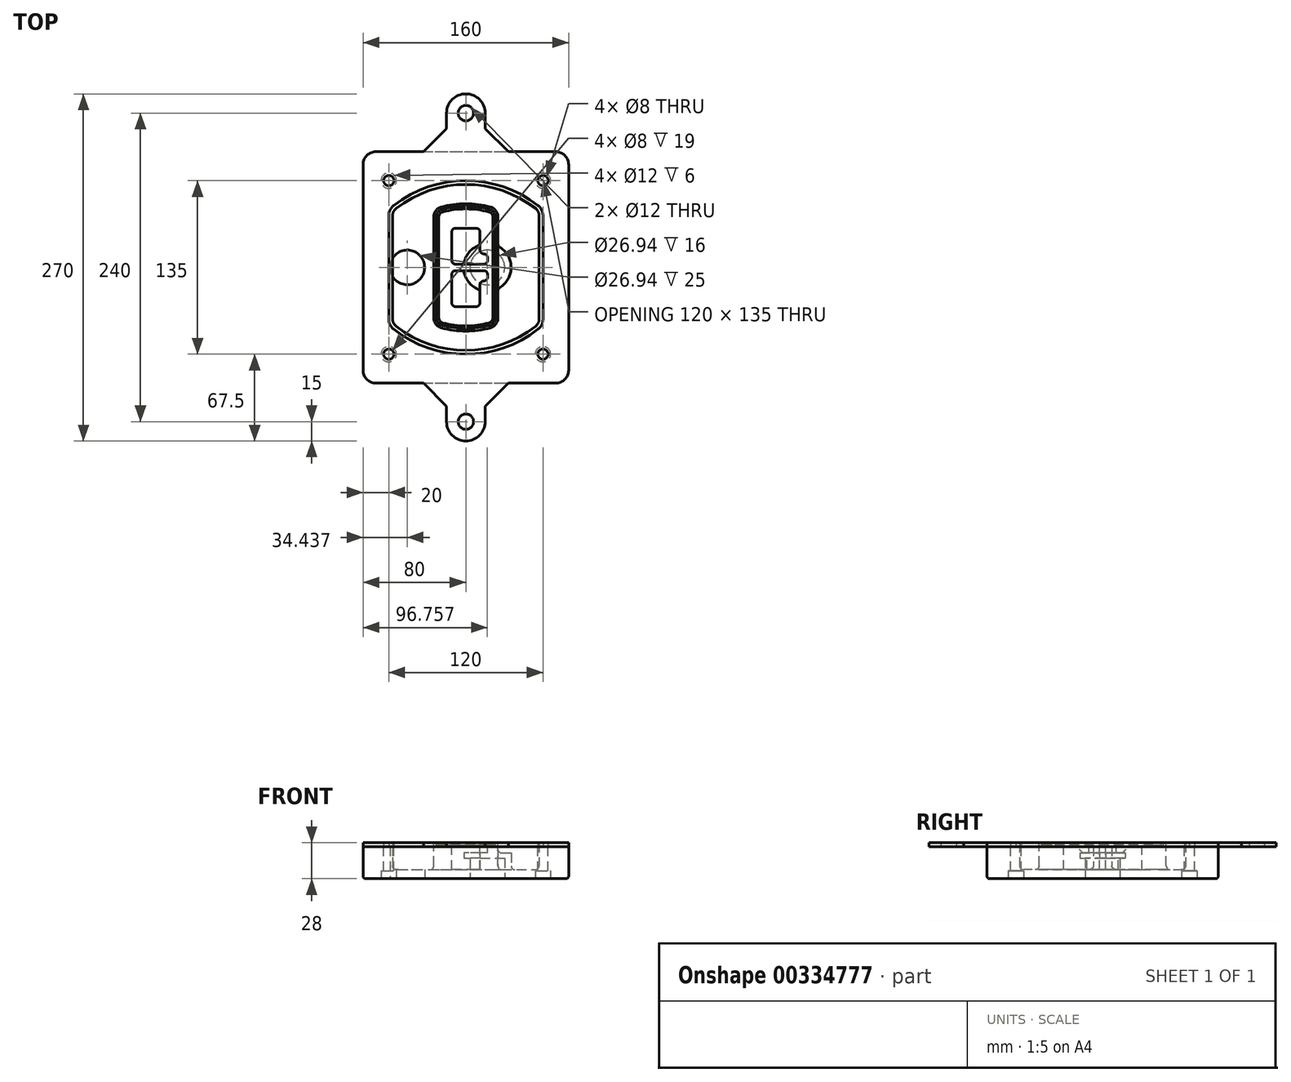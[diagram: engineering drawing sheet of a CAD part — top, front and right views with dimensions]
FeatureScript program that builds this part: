
annotation { "Feature Type Name" : "Feature", "Feature Type Description" : "" }
export const myFeature = defineFeature(function(context is Context, id is Id, definition is map)
    precondition{}
    {
        {
            var Q0;
            Q0=qCreatedBy(makeId("Top.planeOp"),FACE);
            var sketch = newSketch(context, id + "F0", { "sketchPlane" : qUnion([Q0])});
            skPoint(sketch, "E0.rect.middle", {"position": v(0, 0) * mm});
            skLineSegment(sketch, "E1.bottom", {"start": v(-70, -90) * mm, "end": v(70, -90) * mm});
            skLineSegment(sketch, "E1.top", {"start": v(-70, 90) * mm, "end": v(70, 90) * mm});
            skLineSegment(sketch, "E1.left", {"start": v(-80, -80) * mm, "end": v(-80, 80) * mm});
            skLineSegment(sketch, "E1.right", {"start": v(80, -80) * mm, "end": v(80, 80) * mm});
            skLineSegment(sketch, "E2", {"start": v(-80, 90) * mm, "end": v(80, -90) * mm, "construction": true});
            skLineSegment(sketch, "E3", {"start": v(80, 90) * mm, "end": v(-80, -90) * mm, "construction": true});
            skCircle(sketch, "E4", {"center": v(-60, 67.5) * mm, "radius": 4 * mm});
            skCircle(sketch, "E5", {"center": v(60, 67.5) * mm, "radius": 4 * mm});
            skCircle(sketch, "E6", {"center": v(60, -67.5) * mm, "radius": 4 * mm});
            skCircle(sketch, "E7", {"center": v(-60, -67.5) * mm, "radius": 4 * mm});
            skLineSegment(sketch, "E8", {"start": v(-60, 67.5) * mm, "end": v(60, 67.5) * mm, "construction": true});
            skLineSegment(sketch, "E9", {"start": v(60, 67.5) * mm, "end": v(60, -67.5) * mm, "construction": true});
            skLineSegment(sketch, "E10", {"start": v(60, -67.5) * mm, "end": v(-60, -67.5) * mm, "construction": true});
            skLineSegment(sketch, "E11", {"start": v(-60, -67.5) * mm, "end": v(-60, 67.5) * mm, "construction": true});
            skLineSegment(sketch, "E12", {"start": v(-60, 40.3) * mm, "end": v(-60, -40.3) * mm});
            skLineSegment(sketch, "E13", {"start": v(60, 40.3) * mm, "end": v(60, -40.3) * mm});
            skArc(sketch, "E14", {"start": v(56.15, 48.18) * mm, "mid": v(0, 67.5) * mm, "end": v(-56.15, 48.18) * mm});
            skArc(sketch, "E15", {"start": v(-56.15, -48.18) * mm, "mid": v(0, -67.5) * mm, "end": v(56.15, -48.18) * mm});
            skLineSegment(sketch, "E16", {"start": v(-60, 0) * mm, "end": v(60, 0) * mm, "construction": true});
            skPoint(sketch, "E17.visualSharp", {"position": v(-60, -45) * mm});
            skArc(sketch, "E17.filletArc", {"start": v(-60, -40.3) * mm, "mid": v(-58.99, -44.68) * mm, "end": v(-56.15, -48.18) * mm});
            skPoint(sketch, "E18.visualSharp", {"position": v(-60, 45) * mm});
            skArc(sketch, "E18.filletArc", {"start": v(-56.15, 48.18) * mm, "mid": v(-58.99, 44.68) * mm, "end": v(-60, 40.3) * mm});
            skPoint(sketch, "E19.visualSharp", {"position": v(60, 45) * mm});
            skArc(sketch, "E19.filletArc", {"start": v(60, 40.3) * mm, "mid": v(58.99, 44.68) * mm, "end": v(56.15, 48.18) * mm});
            skPoint(sketch, "E20.visualSharp", {"position": v(60, -45) * mm});
            skArc(sketch, "E20.filletArc", {"start": v(56.15, -48.18) * mm, "mid": v(58.99, -44.68) * mm, "end": v(60, -40.3) * mm});
            skPoint(sketch, "E21.visualSharp", {"position": v(-80, 90) * mm});
            skArc(sketch, "E21.filletArc", {"start": v(-70, 90) * mm, "mid": v(-77.07, 87.07) * mm, "end": v(-80, 80) * mm});
            skPoint(sketch, "E22.visualSharp", {"position": v(80, 90) * mm});
            skArc(sketch, "E22.filletArc", {"start": v(80, 80) * mm, "mid": v(77.07, 87.07) * mm, "end": v(70, 90) * mm});
            skPoint(sketch, "E23.visualSharp", {"position": v(80, -90) * mm});
            skArc(sketch, "E23.filletArc", {"start": v(70, -90) * mm, "mid": v(77.07, -87.07) * mm, "end": v(80, -80) * mm});
            skPoint(sketch, "E24.visualSharp", {"position": v(-80, -90) * mm});
            skArc(sketch, "E24.filletArc", {"start": v(-80, -80) * mm, "mid": v(-77.07, -87.07) * mm, "end": v(-70, -90) * mm});
            skArc(sketch, "E25.0", {"start": v(57, 40.3) * mm, "mid": v(56.3, 43.36) * mm, "end": v(54.3, 45.81) * mm});
            skLineSegment(sketch, "E25.1", {"start": v(57, 40.3) * mm, "end": v(57, -40.3) * mm});
            skArc(sketch, "E25.2", {"start": v(54.3, -45.81) * mm, "mid": v(56.3, -43.36) * mm, "end": v(57, -40.3) * mm});
            skArc(sketch, "E25.3", {"start": v(-54.3, -45.81) * mm, "mid": v(0, -64.5) * mm, "end": v(54.3, -45.81) * mm});
            skArc(sketch, "E25.4", {"start": v(-57, -40.3) * mm, "mid": v(-56.3, -43.36) * mm, "end": v(-54.3, -45.81) * mm});
            skArc(sketch, "E25.5", {"start": v(54.3, 45.81) * mm, "mid": v(0, 64.5) * mm, "end": v(-54.3, 45.81) * mm});
            skLineSegment(sketch, "E25.6", {"start": v(-57, 40.3) * mm, "end": v(-57, -40.3) * mm});
            skArc(sketch, "E25.7", {"start": v(-54.3, 45.81) * mm, "mid": v(-56.3, 43.36) * mm, "end": v(-57, 40.3) * mm});
            skArc(sketch, "E26.0", {"start": v(-58.62, 51.33) * mm, "mid": v(-62.58, 46.43) * mm, "end": v(-64, 40.3) * mm});
            skArc(sketch, "E26.1", {"start": v(58.62, 51.33) * mm, "mid": v(0, 71.5) * mm, "end": v(-58.62, 51.33) * mm});
            skArc(sketch, "E26.2", {"start": v(64, 40.3) * mm, "mid": v(62.58, 46.43) * mm, "end": v(58.62, 51.33) * mm});
            skLineSegment(sketch, "E26.3", {"start": v(64, 40.3) * mm, "end": v(64, -40.3) * mm});
            skArc(sketch, "E26.4", {"start": v(58.62, -51.33) * mm, "mid": v(62.58, -46.43) * mm, "end": v(64, -40.3) * mm});
            skLineSegment(sketch, "E26.5", {"start": v(-64, 40.3) * mm, "end": v(-64, -40.3) * mm});
            skArc(sketch, "E26.6", {"start": v(-58.62, -51.33) * mm, "mid": v(0, -71.5) * mm, "end": v(58.62, -51.33) * mm});
            skArc(sketch, "E26.7", {"start": v(-64, -40.3) * mm, "mid": v(-62.58, -46.43) * mm, "end": v(-58.62, -51.33) * mm});
            skSolve(sketch);
        }
        {
            var Q0;
            Q0=makeQuery(id+"F0.imprint","IMPRINT",FACE,{"disambiguationData":[TD([[makeQuery(id+"F0.imprint","IMPRINT",EDGE,{"derivedFrom":sQuery(id+"F0.wireOp",EDGE,"E1.bottom")}),1.0]])]});
            var Q1;
            Q1=makeQuery(id+"F0.imprint","IMPRINT",FACE,{"disambiguationData":[TD([[makeQuery(id+"F0.imprint","IMPRINT",EDGE,{"derivedFrom":sQuery(id+"F0.wireOp",EDGE,"E12")}),1.0]])]});
            var Q2;
            Q2=makeQuery(id+"F0.imprint","IMPRINT",FACE,{"disambiguationData":[TD([[makeQuery(id+"F0.imprint","IMPRINT",EDGE,{"derivedFrom":sQuery(id+"F0.wireOp",EDGE,"E25.0")}),1.0]])]});
            var Q3;
            Q3=makeQuery(id+"F0.imprint","IMPRINT",FACE,{"disambiguationData":[TD([[makeQuery(id+"F0.imprint","IMPRINT",EDGE,{"derivedFrom":sQuery(id+"F0.wireOp",EDGE,"E12")}),-1.0]])]});
            extrude(context, id + "F1", {"entities" : qUnion([Q0, Q1, Q2, Q3]), "oppositeDirection" : true, "depth" : 25 * mm});
        }
        {
            var Q0;
            Q0=makeQuery(id+"F0.imprint","IMPRINT",FACE,{"disambiguationData":[TD([[makeQuery(id+"F0.imprint","IMPRINT",EDGE,{"derivedFrom":sQuery(id+"F0.wireOp",EDGE,"E12")}),1.0]])]});
            extrude(context, id + "F2", {"entities" : qUnion([Q0]), "operationType" : NewBodyOperationType.ADD, "depth" : 3 * mm});
        }
        {
            var Q0;
            Q0=makeQuery(id+"F0.imprint","IMPRINT",FACE,{"disambiguationData":[TD([[makeQuery(id+"F0.imprint","IMPRINT",EDGE,{"derivedFrom":sQuery(id+"F0.wireOp",EDGE,"E25.0")}),1.0]])]});
            extrude(context, id + "F3", {"entities" : qUnion([Q0]), "operationType" : NewBodyOperationType.REMOVE, "oppositeDirection" : true, "depth" : 18 * mm});
        }
        {
            var Q0;
            Q0=makeQuery(id+"F2.opExtrude","CAP_FACE",FACE,{"disambiguationData":[OSD([sQuery(id+"F0.wireOp",EDGE,"E12"),sQuery(id+"F0.wireOp",EDGE,"E13"),sQuery(id+"F0.wireOp",EDGE,"E14"),sQuery(id+"F0.wireOp",EDGE,"E15"),sQuery(id+"F0.wireOp",EDGE,"E17.filletArc"),sQuery(id+"F0.wireOp",EDGE,"E18.filletArc"),sQuery(id+"F0.wireOp",EDGE,"E19.filletArc"),sQuery(id+"F0.wireOp",EDGE,"E20.filletArc"),sQuery(id+"F0.wireOp",EDGE,"E25.0"),sQuery(id+"F0.wireOp",EDGE,"E25.1"),sQuery(id+"F0.wireOp",EDGE,"E25.2"),sQuery(id+"F0.wireOp",EDGE,"E25.3"),sQuery(id+"F0.wireOp",EDGE,"E25.4"),sQuery(id+"F0.wireOp",EDGE,"E25.5"),sQuery(id+"F0.wireOp",EDGE,"E25.6"),sQuery(id+"F0.wireOp",EDGE,"E25.7")])],"isStart":false});
            var sketch = newSketch(context, id + "F4", { "sketchPlane" : qUnion([Q0])});
            skArc(sketch, "E27.0", {"start": v(-19.08, -46.97) * mm, "mid": v(0, -49.5) * mm, "end": v(19.08, -46.97) * mm});
            skArc(sketch, "E28.0", {"start": v(19.08, 46.97) * mm, "mid": v(0, 49.5) * mm, "end": v(-19.08, 46.97) * mm});
            skLineSegment(sketch, "E29", {"start": v(-25, 39.25) * mm, "end": v(-25, -39.25) * mm});
            skLineSegment(sketch, "E30", {"start": v(25, 39.25) * mm, "end": v(25, -39.25) * mm});
            skLineSegment(sketch, "E31", {"start": v(-25, 45.1) * mm, "end": v(25, 45.1) * mm, "construction": true});
            skLineSegment(sketch, "E32", {"start": v(-25, -45.1) * mm, "end": v(25, -45.1) * mm, "construction": true});
            skPoint(sketch, "E33.visualSharp", {"position": v(-25, 45.1) * mm});
            skArc(sketch, "E33.filletArc", {"start": v(-19.08, 46.97) * mm, "mid": v(-23.35, 44.11) * mm, "end": v(-25, 39.25) * mm});
            skPoint(sketch, "E34.visualSharp", {"position": v(25, 45.1) * mm});
            skArc(sketch, "E34.filletArc", {"start": v(25, 39.25) * mm, "mid": v(23.35, 44.11) * mm, "end": v(19.08, 46.97) * mm});
            skPoint(sketch, "E35.visualSharp", {"position": v(25, -45.1) * mm});
            skArc(sketch, "E35.filletArc", {"start": v(19.08, -46.97) * mm, "mid": v(23.35, -44.11) * mm, "end": v(25, -39.25) * mm});
            skPoint(sketch, "E36.visualSharp", {"position": v(-25, -45.1) * mm});
            skArc(sketch, "E36.filletArc", {"start": v(-25, -39.25) * mm, "mid": v(-23.35, -44.11) * mm, "end": v(-19.08, -46.97) * mm});
            skArc(sketch, "E37.0", {"start": v(54.3, 45.81) * mm, "mid": v(0, 64.5) * mm, "end": v(-54.3, 45.81) * mm});
            skArc(sketch, "E37.1", {"start": v(-54.3, 45.81) * mm, "mid": v(-56.3, 43.36) * mm, "end": v(-57, 40.3) * mm});
            skLineSegment(sketch, "E37.2", {"start": v(-57, 40.3) * mm, "end": v(-57, -40.3) * mm});
            skArc(sketch, "E37.3", {"start": v(-57, -40.3) * mm, "mid": v(-56.3, -43.36) * mm, "end": v(-54.3, -45.81) * mm});
            skArc(sketch, "E37.4", {"start": v(-54.3, -45.81) * mm, "mid": v(0, -64.5) * mm, "end": v(54.3, -45.81) * mm});
            skArc(sketch, "E37.5", {"start": v(54.3, -45.81) * mm, "mid": v(56.3, -43.36) * mm, "end": v(57, -40.3) * mm});
            skLineSegment(sketch, "E37.6", {"start": v(57, 40.3) * mm, "end": v(57, -40.3) * mm});
            skArc(sketch, "E37.7", {"start": v(57, 40.3) * mm, "mid": v(56.3, 43.36) * mm, "end": v(54.3, 45.81) * mm});
            skLineSegment(sketch, "E38.0", {"start": v(23, 39.25) * mm, "end": v(23, -39.25) * mm});
            skArc(sketch, "E38.1", {"start": v(18.56, -45.04) * mm, "mid": v(21.76, -42.9) * mm, "end": v(23, -39.25) * mm});
            skArc(sketch, "E38.2", {"start": v(-18.56, -45.04) * mm, "mid": v(0, -47.5) * mm, "end": v(18.56, -45.04) * mm});
            skArc(sketch, "E38.3", {"start": v(-23, -39.25) * mm, "mid": v(-21.76, -42.9) * mm, "end": v(-18.56, -45.04) * mm});
            skLineSegment(sketch, "E38.4", {"start": v(-23, 39.25) * mm, "end": v(-23, -39.25) * mm});
            skArc(sketch, "E38.5", {"start": v(23, 39.25) * mm, "mid": v(21.76, 42.9) * mm, "end": v(18.56, 45.04) * mm});
            skArc(sketch, "E38.6", {"start": v(-18.56, 45.04) * mm, "mid": v(-21.76, 42.9) * mm, "end": v(-23, 39.25) * mm});
            skArc(sketch, "E38.7", {"start": v(18.56, 45.04) * mm, "mid": v(0, 47.5) * mm, "end": v(-18.56, 45.04) * mm});
            skArc(sketch, "E39.0", {"start": v(21, 39.25) * mm, "mid": v(20.18, 41.68) * mm, "end": v(18.04, 43.1) * mm});
            skLineSegment(sketch, "E39.1", {"start": v(21, 39.25) * mm, "end": v(21, -39.25) * mm});
            skArc(sketch, "E39.2", {"start": v(18.04, -43.1) * mm, "mid": v(20.18, -41.68) * mm, "end": v(21, -39.25) * mm});
            skArc(sketch, "E39.3", {"start": v(-18.04, -43.1) * mm, "mid": v(0, -45.5) * mm, "end": v(18.04, -43.1) * mm});
            skArc(sketch, "E39.4", {"start": v(-21, -39.25) * mm, "mid": v(-20.18, -41.68) * mm, "end": v(-18.04, -43.1) * mm});
            skArc(sketch, "E39.5", {"start": v(18.04, 43.1) * mm, "mid": v(0, 45.5) * mm, "end": v(-18.04, 43.1) * mm});
            skLineSegment(sketch, "E39.6", {"start": v(-21, 39.25) * mm, "end": v(-21, -39.25) * mm});
            skArc(sketch, "E39.7", {"start": v(-18.04, 43.1) * mm, "mid": v(-20.18, 41.68) * mm, "end": v(-21, 39.25) * mm});
            skLineSegment(sketch, "E40", {"start": v(-25, 0) * mm, "end": v(25, 0) * mm, "construction": true});
            skLineSegment(sketch, "E41", {"start": v(-11, 5.5) * mm, "end": v(-11, 27.5) * mm});
            skLineSegment(sketch, "E42", {"start": v(-8, 30.5) * mm, "end": v(8, 30.5) * mm});
            skLineSegment(sketch, "E43", {"start": v(11, 27.5) * mm, "end": v(11, 13.5) * mm});
            skLineSegment(sketch, "E44", {"start": v(14, 10.5) * mm, "end": v(14, 10.5) * mm});
            skLineSegment(sketch, "E45", {"start": v(17, 7.5) * mm, "end": v(17, 5.5) * mm});
            skLineSegment(sketch, "E46", {"start": v(14, 2.5) * mm, "end": v(-8, 2.5) * mm});
            skPoint(sketch, "E47.visualSharp", {"position": v(-11, 30.5) * mm});
            skArc(sketch, "E47.filletArc", {"start": v(-8, 30.5) * mm, "mid": v(-10.12, 29.62) * mm, "end": v(-11, 27.5) * mm});
            skPoint(sketch, "E48.visualSharp", {"position": v(11, 30.5) * mm});
            skArc(sketch, "E48.filletArc", {"start": v(11, 27.5) * mm, "mid": v(10.12, 29.62) * mm, "end": v(8, 30.5) * mm});
            skPoint(sketch, "E49.visualSharp", {"position": v(11, 10.5) * mm});
            skArc(sketch, "E49.filletArc", {"start": v(11, 13.5) * mm, "mid": v(11.88, 11.38) * mm, "end": v(14, 10.5) * mm});
            skPoint(sketch, "E50.visualSharp", {"position": v(17, 10.5) * mm});
            skArc(sketch, "E50.filletArc", {"start": v(17, 7.5) * mm, "mid": v(16.12, 9.62) * mm, "end": v(14, 10.5) * mm});
            skPoint(sketch, "E51.visualSharp", {"position": v(17, 2.5) * mm});
            skArc(sketch, "E51.filletArc", {"start": v(14, 2.5) * mm, "mid": v(16.12, 3.38) * mm, "end": v(17, 5.5) * mm});
            skPoint(sketch, "E52.visualSharp", {"position": v(-11, 2.5) * mm});
            skArc(sketch, "E52.filletArc", {"start": v(-11, 5.5) * mm, "mid": v(-10.12, 3.38) * mm, "end": v(-8, 2.5) * mm});
            skLineSegment(sketch, "E53.0.MirrorCS", {"start": v(14, -2.5) * mm, "end": v(-8, -2.5) * mm});
            skArc(sketch, "E54.0.MirrorCS", {"start": v(-11, -5.5) * mm, "mid": v(-10.12, -3.38) * mm, "end": v(-8, -2.5) * mm});
            skLineSegment(sketch, "E55.0.MirrorCS", {"start": v(-11, -5.5) * mm, "end": v(-11, -27.5) * mm});
            skArc(sketch, "E56.0.MirrorCS", {"start": v(-8, -30.5) * mm, "mid": v(-10.12, -29.62) * mm, "end": v(-11, -27.5) * mm});
            skLineSegment(sketch, "E57.0.MirrorCS", {"start": v(-8, -30.5) * mm, "end": v(8, -30.5) * mm});
            skArc(sketch, "E58.0.MirrorCS", {"start": v(11, -27.5) * mm, "mid": v(10.12, -29.62) * mm, "end": v(8, -30.5) * mm});
            skLineSegment(sketch, "E59.0.MirrorCS", {"start": v(11, -27.5) * mm, "end": v(11, -13.5) * mm});
            skArc(sketch, "E60.0.MirrorCS", {"start": v(11, -13.5) * mm, "mid": v(11.88, -11.38) * mm, "end": v(14, -10.5) * mm});
            skArc(sketch, "E61.0.MirrorCS", {"start": v(17, -7.5) * mm, "mid": v(16.12, -9.62) * mm, "end": v(14, -10.5) * mm});
            skLineSegment(sketch, "E62.0.MirrorCS", {"start": v(17, -7.5) * mm, "end": v(17, -5.5) * mm});
            skArc(sketch, "E63.0.MirrorCS", {"start": v(14, -2.5) * mm, "mid": v(16.12, -3.38) * mm, "end": v(17, -5.5) * mm});
            skSolve(sketch);
        }
        {
            var Q0;
            Q0=makeQuery(id+"F4.imprint","IMPRINT",FACE,{"disambiguationData":[TD([[makeQuery(id+"F4.imprint","IMPRINT",EDGE,{"derivedFrom":sQuery(id+"F4.wireOp",EDGE,"E27.0")}),1.0]])]});
            var Q1;
            Q1=makeQuery(id+"F4.imprint","IMPRINT",FACE,{"disambiguationData":[TD([[makeQuery(id+"F4.imprint","IMPRINT",EDGE,{"derivedFrom":sQuery(id+"F4.wireOp",EDGE,"E38.0")}),-1.0]])]});
            var Q2;
            Q2=makeQuery(id+"F4.imprint","IMPRINT",FACE,{"disambiguationData":[TD([[makeQuery(id+"F4.imprint","IMPRINT",EDGE,{"derivedFrom":sQuery(id+"F4.wireOp",EDGE,"E39.0")}),1.0]])]});
            extrude(context, id + "F5", {"entities" : qUnion([Q0, Q1, Q2]), "operationType" : NewBodyOperationType.ADD, "endBound" : BoundingType.UP_TO_NEXT, "oppositeDirection" : true, "depth" : 25 * mm});
        }
        {
            var Q0;
            Q0=makeQuery(id+"F4.imprint","IMPRINT",FACE,{"disambiguationData":[TD([[makeQuery(id+"F4.imprint","IMPRINT",EDGE,{"derivedFrom":sQuery(id+"F4.wireOp",EDGE,"E38.0")}),-1.0]])]});
            extrude(context, id + "F6", {"entities" : qUnion([Q0]), "operationType" : NewBodyOperationType.REMOVE, "oppositeDirection" : true, "depth" : 2 * mm});
        }
        {
            var Q0;
            Q0=makeQuery(id+"F1.opExtrude","CAP_FACE",FACE,{"disambiguationData":[OSD([sQuery(id+"F0.wireOp",EDGE,"E1.bottom"),sQuery(id+"F0.wireOp",EDGE,"E1.top"),sQuery(id+"F0.wireOp",EDGE,"E1.left"),sQuery(id+"F0.wireOp",EDGE,"E1.right"),sQuery(id+"F0.wireOp",EDGE,"E4"),sQuery(id+"F0.wireOp",EDGE,"E5"),sQuery(id+"F0.wireOp",EDGE,"E6"),sQuery(id+"F0.wireOp",EDGE,"E7"),sQuery(id+"F0.wireOp",EDGE,"E21.filletArc"),sQuery(id+"F0.wireOp",EDGE,"E22.filletArc"),sQuery(id+"F0.wireOp",EDGE,"E23.filletArc"),sQuery(id+"F0.wireOp",EDGE,"E24.filletArc")])],"isStart":false});
            var sketch = newSketch(context, id + "F7", { "sketchPlane" : qUnion([Q0])});
            skCircle(sketch, "E64", {"center": v(16.76, 0) * mm, "radius": 13.47 * mm});
            skCircle(sketch, "E65", {"center": v(-45.56, 0) * mm, "radius": 13.47 * mm});
            skLineSegment(sketch, "E66", {"start": v(80, 0) * mm, "end": v(-80, 0) * mm});
            skCircle(sketch, "E67", {"center": v(16.76, 0) * mm, "radius": 18.47 * mm});
            skCircle(sketch, "E68", {"center": v(60, -67.5) * mm, "radius": 6 * mm});
            skCircle(sketch, "E69", {"center": v(-60, -67.5) * mm, "radius": 6 * mm});
            skCircle(sketch, "E70", {"center": v(-60, 67.5) * mm, "radius": 6 * mm});
            skCircle(sketch, "E71", {"center": v(60, 67.5) * mm, "radius": 6 * mm});
            skSolve(sketch);
        }
        {
            var Q0;
            {var subQ1=sQuery(id+"F7.wireOp",EDGE,"E66");var subQ4=sQuery(id+"F7.wireOp",EDGE,"E64");var subQ6=makeQuery(id+"F7.imprint","INTERSECT",VERTEX,{"disambiguationData":[OD(0.0)],"derivedFrom":[subQ4,subQ1]});Q0=makeQuery(id+"F7.imprint","IMPRINT",FACE,{"disambiguationData":[TD([[makeQuery(id+"F7.imprint","IMPRINT",EDGE,{"disambiguationData":[TD([[subQ6,-1.0]])],"derivedFrom":subQ4}),-1.0]])]});}
            var Q1;
            {var subQ0=sQuery(id+"F7.wireOp",EDGE,"E66");var subQ1=sQuery(id+"F7.wireOp",EDGE,"E64");var subQ3=makeQuery(id+"F7.imprint","INTERSECT",VERTEX,{"disambiguationData":[OD(0.0)],"derivedFrom":[subQ1,subQ0]});Q1=makeQuery(id+"F7.imprint","IMPRINT",FACE,{"disambiguationData":[TD([[makeQuery(id+"F7.imprint","IMPRINT",EDGE,{"disambiguationData":[TD([[subQ3,-1.0]])],"derivedFrom":subQ1}),1.0]])]});}
            var Q2;
            {var subQ0=sQuery(id+"F7.wireOp",EDGE,"E66");var subQ1=sQuery(id+"F7.wireOp",EDGE,"E64");var subQ3=makeQuery(id+"F7.imprint","INTERSECT",VERTEX,{"disambiguationData":[OD(0.0)],"derivedFrom":[subQ1,subQ0]});Q2=makeQuery(id+"F7.imprint","IMPRINT",FACE,{"disambiguationData":[TD([[makeQuery(id+"F7.imprint","IMPRINT",EDGE,{"disambiguationData":[TD([[subQ3,1.0]])],"derivedFrom":subQ1}),1.0]])]});}
            var Q3;
            {var subQ1=sQuery(id+"F7.wireOp",EDGE,"E66");var subQ4=sQuery(id+"F7.wireOp",EDGE,"E64");var subQ6=makeQuery(id+"F7.imprint","INTERSECT",VERTEX,{"disambiguationData":[OD(0.0)],"derivedFrom":[subQ4,subQ1]});Q3=makeQuery(id+"F7.imprint","IMPRINT",FACE,{"disambiguationData":[TD([[makeQuery(id+"F7.imprint","IMPRINT",EDGE,{"disambiguationData":[TD([[subQ6,1.0]])],"derivedFrom":subQ4}),-1.0]])]});}
            extrude(context, id + "F8", {"entities" : qUnion([Q0, Q1, Q2, Q3]), "operationType" : NewBodyOperationType.ADD, "oppositeDirection" : true, "depth" : 20 * mm});
        }
        {
            var Q0;
            {var subQ0=sQuery(id+"F7.wireOp",EDGE,"E66");var subQ1=sQuery(id+"F7.wireOp",EDGE,"E64");var subQ3=makeQuery(id+"F7.imprint","INTERSECT",VERTEX,{"disambiguationData":[OD(0.0)],"derivedFrom":[subQ1,subQ0]});Q0=makeQuery(id+"F7.imprint","IMPRINT",FACE,{"disambiguationData":[TD([[makeQuery(id+"F7.imprint","IMPRINT",EDGE,{"disambiguationData":[TD([[subQ3,-1.0]])],"derivedFrom":subQ1}),1.0]])]});}
            var Q1;
            {var subQ0=sQuery(id+"F7.wireOp",EDGE,"E66");var subQ1=sQuery(id+"F7.wireOp",EDGE,"E64");var subQ3=makeQuery(id+"F7.imprint","INTERSECT",VERTEX,{"disambiguationData":[OD(0.0)],"derivedFrom":[subQ1,subQ0]});Q1=makeQuery(id+"F7.imprint","IMPRINT",FACE,{"disambiguationData":[TD([[makeQuery(id+"F7.imprint","IMPRINT",EDGE,{"disambiguationData":[TD([[subQ3,1.0]])],"derivedFrom":subQ1}),1.0]])]});}
            extrude(context, id + "F9", {"entities" : qUnion([Q0, Q1]), "operationType" : NewBodyOperationType.REMOVE, "oppositeDirection" : true, "depth" : 16 * mm});
        }
        {
            var Q0;
            {var subQ0=sQuery(id+"F7.wireOp",EDGE,"E66");var subQ1=sQuery(id+"F7.wireOp",EDGE,"E65");var subQ3=makeQuery(id+"F7.imprint","INTERSECT",VERTEX,{"disambiguationData":[OD(0.0)],"derivedFrom":[subQ1,subQ0]});Q0=makeQuery(id+"F7.imprint","IMPRINT",FACE,{"disambiguationData":[TD([[makeQuery(id+"F7.imprint","IMPRINT",EDGE,{"disambiguationData":[TD([[subQ3,-1.0]])],"derivedFrom":subQ1}),1.0]])]});}
            var Q1;
            {var subQ0=sQuery(id+"F7.wireOp",EDGE,"E66");var subQ1=sQuery(id+"F7.wireOp",EDGE,"E65");var subQ3=makeQuery(id+"F7.imprint","INTERSECT",VERTEX,{"disambiguationData":[OD(0.0)],"derivedFrom":[subQ1,subQ0]});Q1=makeQuery(id+"F7.imprint","IMPRINT",FACE,{"disambiguationData":[TD([[makeQuery(id+"F7.imprint","IMPRINT",EDGE,{"disambiguationData":[TD([[subQ3,1.0]])],"derivedFrom":subQ1}),1.0]])]});}
            extrude(context, id + "F10", {"entities" : qUnion([Q0, Q1]), "operationType" : NewBodyOperationType.REMOVE, "oppositeDirection" : true, "depth" : 25 * mm});
        }
        {
            var Q0;
            Q0=makeQuery(id+"F7.imprint","IMPRINT",FACE,{"disambiguationData":[TD([[makeQuery(id+"F7.imprint","IMPRINT",EDGE,{"derivedFrom":sQuery(id+"F7.wireOp",EDGE,"E68")}),1.0]])]});
            var Q1;
            Q1=makeQuery(id+"F7.imprint","IMPRINT",FACE,{"disambiguationData":[TD([[makeQuery(id+"F7.imprint","IMPRINT",EDGE,{"derivedFrom":makeQuery(id+"F1.opExtrude","CAP_EDGE",EDGE,{"disambiguationData":[OSD([sQuery(id+"F0.wireOp",EDGE,"E5")])],"isStart":false})}),-1.0]])]});
            var Q2;
            Q2=makeQuery(id+"F7.imprint","IMPRINT",FACE,{"disambiguationData":[TD([[makeQuery(id+"F7.imprint","IMPRINT",EDGE,{"derivedFrom":sQuery(id+"F7.wireOp",EDGE,"E69")}),1.0]])]});
            var Q3;
            Q3=makeQuery(id+"F7.imprint","IMPRINT",FACE,{"disambiguationData":[TD([[makeQuery(id+"F7.imprint","IMPRINT",EDGE,{"derivedFrom":makeQuery(id+"F1.opExtrude","CAP_EDGE",EDGE,{"disambiguationData":[OSD([sQuery(id+"F0.wireOp",EDGE,"E4")])],"isStart":false})}),-1.0]])]});
            var Q4;
            Q4=makeQuery(id+"F7.imprint","IMPRINT",FACE,{"disambiguationData":[TD([[makeQuery(id+"F7.imprint","IMPRINT",EDGE,{"derivedFrom":sQuery(id+"F7.wireOp",EDGE,"E70")}),1.0]])]});
            var Q5;
            Q5=makeQuery(id+"F7.imprint","IMPRINT",FACE,{"disambiguationData":[TD([[makeQuery(id+"F7.imprint","IMPRINT",EDGE,{"derivedFrom":makeQuery(id+"F1.opExtrude","CAP_EDGE",EDGE,{"disambiguationData":[OSD([sQuery(id+"F0.wireOp",EDGE,"E7")])],"isStart":false})}),-1.0]])]});
            var Q6;
            Q6=makeQuery(id+"F7.imprint","IMPRINT",FACE,{"disambiguationData":[TD([[makeQuery(id+"F7.imprint","IMPRINT",EDGE,{"derivedFrom":sQuery(id+"F7.wireOp",EDGE,"E71")}),1.0]])]});
            var Q7;
            Q7=makeQuery(id+"F7.imprint","IMPRINT",FACE,{"disambiguationData":[TD([[makeQuery(id+"F7.imprint","IMPRINT",EDGE,{"derivedFrom":makeQuery(id+"F1.opExtrude","CAP_EDGE",EDGE,{"disambiguationData":[OSD([sQuery(id+"F0.wireOp",EDGE,"E6")])],"isStart":false})}),-1.0]])]});
            extrude(context, id + "F11", {"entities" : qUnion([Q0, Q1, Q2, Q3, Q4, Q5, Q6, Q7]), "operationType" : NewBodyOperationType.REMOVE, "oppositeDirection" : true, "depth" : 6 * mm});
        }
        {
            var Q0;
            Q0=makeQuery(id+"F9.boolean.opBoolean","COPY",FACE,{"derivedFrom":makeQuery(id+"F9.opExtrude","CAP_FACE",FACE,{"disambiguationData":[OSD([sQuery(id+"F7.wireOp",EDGE,"E64")])],"isStart":false})});
            var sketch = newSketch(context, id + "F12", { "sketchPlane" : qUnion([Q0])});
            skArc(sketch, "E72.0", {"start": v(11, 17.55) * mm, "mid": v(2.57, 11.82) * mm, "end": v(-1.54, 2.5) * mm});
            skArc(sketch, "E72.1", {"start": v(-1.54, -2.5) * mm, "mid": v(2.57, -11.82) * mm, "end": v(11, -17.55) * mm});
            skLineSegment(sketch, "E73", {"start": v(-1.54, -2.5) * mm, "end": v(14, -2.5) * mm});
            skLineSegment(sketch, "E74.0", {"start": v(14, 2.5) * mm, "end": v(-1.54, 2.5) * mm});
            skArc(sketch, "E74.1", {"start": v(14, 2.5) * mm, "mid": v(16.12, 3.38) * mm, "end": v(17, 5.5) * mm});
            skLineSegment(sketch, "E74.2", {"start": v(17, 7.5) * mm, "end": v(17, 5.5) * mm});
            skArc(sketch, "E74.3", {"start": v(17, 7.5) * mm, "mid": v(16.12, 9.62) * mm, "end": v(14, 10.5) * mm});
            skArc(sketch, "E74.4", {"start": v(11, 13.5) * mm, "mid": v(11.88, 11.38) * mm, "end": v(14, 10.5) * mm});
            skLineSegment(sketch, "E74.5", {"start": v(11, 17.55) * mm, "end": v(11, 13.5) * mm});
            skLineSegment(sketch, "E74.7", {"start": v(14, -2.5) * mm, "end": v(-1.54, -2.5) * mm});
            skArc(sketch, "E74.8", {"start": v(14, -2.5) * mm, "mid": v(16.12, -3.38) * mm, "end": v(17, -5.5) * mm});
            skLineSegment(sketch, "E74.9", {"start": v(17, -7.5) * mm, "end": v(17, -5.5) * mm});
            skArc(sketch, "E74.10", {"start": v(17, -7.5) * mm, "mid": v(16.12, -9.62) * mm, "end": v(14, -10.5) * mm});
            skArc(sketch, "E74.11", {"start": v(11, -13.5) * mm, "mid": v(11.88, -11.38) * mm, "end": v(14, -10.5) * mm});
            skLineSegment(sketch, "E74.12", {"start": v(11, -17.55) * mm, "end": v(11, -13.5) * mm});
            skPoint(sketch, "E75.orphan", {"position": v(11, -27.5) * mm});
            skPoint(sketch, "E76.orphan", {"position": v(-8, -2.5) * mm});
            skPoint(sketch, "E77.orphan", {"position": v(-8, 2.5) * mm});
            skPoint(sketch, "E78.orphan", {"position": v(11, 27.5) * mm});
            skSolve(sketch);
        }
        {
            var Q0;
            {var subQ7=sQuery(id+"F12.wireOp",EDGE,"E72.0");var subQ14=sQuery(id+"F12.wireOp",EDGE,"E72.1");var subQ16=sQuery(id+"F12.wireOp",EDGE,"E74.1");var subQ18=sQuery(id+"F12.wireOp",EDGE,"E74.8");Q0=qUnion([makeQuery(id+"F12.imprint","IMPRINT",FACE,{"disambiguationData":[TD([[makeQuery(id+"F12.imprint","IMPRINT",EDGE,{"derivedFrom":subQ7}),1.0]])]}),makeQuery(id+"F12.imprint","IMPRINT",FACE,{"disambiguationData":[TD([[makeQuery(id+"F12.imprint","IMPRINT",EDGE,{"derivedFrom":subQ14}),1.0]])]}),makeQuery(id+"F12.imprint","IMPRINT",FACE,{"disambiguationData":[TD([[makeQuery(id+"F12.imprint","IMPRINT",EDGE,{"derivedFrom":subQ16}),1.0]])]}),makeQuery(id+"F12.imprint","IMPRINT",FACE,{"disambiguationData":[TD([[makeQuery(id+"F12.imprint","IMPRINT",EDGE,{"derivedFrom":subQ18}),-1.0]])]})]);}
            var Q1;
            Q1=makeQuery(id+"F5.boolean.opBoolean","SPLIT",FACE,{"disambiguationData":[TD([makeQuery(id+"F5.opExtrude","SWEPT_FACE",FACE,{"disambiguationData":[OSD([sQuery(id+"F4.wireOp",EDGE,"E41")])]})])],"derivedFrom":makeQuery(id+"F3.boolean.opBoolean","COPY",FACE,{"derivedFrom":makeQuery(id+"F3.opExtrude","CAP_FACE",FACE,{"disambiguationData":[OSD([sQuery(id+"F0.wireOp",EDGE,"E25.0"),sQuery(id+"F0.wireOp",EDGE,"E25.1"),sQuery(id+"F0.wireOp",EDGE,"E25.2"),sQuery(id+"F0.wireOp",EDGE,"E25.3"),sQuery(id+"F0.wireOp",EDGE,"E25.4"),sQuery(id+"F0.wireOp",EDGE,"E25.5"),sQuery(id+"F0.wireOp",EDGE,"E25.6"),sQuery(id+"F0.wireOp",EDGE,"E25.7")])],"isStart":false})})});
            extrude(context, id + "F13", {"entities" : qUnion([Q0]), "operationType" : NewBodyOperationType.REMOVE, "endBound" : BoundingType.UP_TO_SURFACE, "endBoundEntityFace" : qUnion([Q1]), "depth" : 25 * mm});
        }
        {
            var Q0;
            Q0=makeQuery(id+"F3.boolean.opBoolean","COPY",EDGE,{"derivedFrom":makeQuery(id+"F3.opExtrude","CAP_EDGE",EDGE,{"disambiguationData":[OSD([sQuery(id+"F0.wireOp",EDGE,"E25.6")])],"isStart":false})});
            var Q1;
            Q1=makeQuery(id+"F8.boolean.opBoolean","INTERSECT",EDGE,{"derivedFrom":[makeQuery(id+"F5.opExtrude","SWEPT_FACE",FACE,{"disambiguationData":[OSD([sQuery(id+"F4.wireOp",EDGE,"E30")])]}),makeQuery(id+"F8.opExtrude","CAP_FACE",FACE,{"disambiguationData":[OSD([sQuery(id+"F7.wireOp",EDGE,"E67")])],"isStart":false})]});
            var Q2;
            Q2=makeQuery(id+"F8.boolean.opBoolean","INTERSECT",EDGE,{"disambiguationData":[OD(1.0)],"derivedFrom":[makeQuery(id+"F5.opExtrude","SWEPT_FACE",FACE,{"disambiguationData":[OSD([sQuery(id+"F4.wireOp",EDGE,"E30")])]}),makeQuery(id+"F8.opExtrude","SWEPT_FACE",FACE,{"disambiguationData":[OSD([sQuery(id+"F7.wireOp",EDGE,"E67")])]})]});
            var Q3;
            {var subQ0=sQuery(id+"F4.wireOp",EDGE,"E30");Q3=makeQuery(id+"F8.boolean.opBoolean","SPLIT",EDGE,{"disambiguationData":[TD([makeQuery(id+"F5.opExtrude","SWEPT_FACE",FACE,{"disambiguationData":[OSD([sQuery(id+"F4.wireOp",EDGE,"E35.filletArc")])]})])],"derivedFrom":makeQuery(id+"F5.opExtrude","CAP_EDGE",EDGE,{"disambiguationData":[OSD([subQ0])],"isStart":false})});}
            var Q4;
            {var subQ0=sQuery(id+"F0.wireOp",EDGE,"E25.7");var subQ1=sQuery(id+"F0.wireOp",EDGE,"E25.1");var subQ2=sQuery(id+"F0.wireOp",EDGE,"E25.6");var subQ3=sQuery(id+"F0.wireOp",EDGE,"E25.5");var subQ4=sQuery(id+"F0.wireOp",EDGE,"E25.4");var subQ5=sQuery(id+"F0.wireOp",EDGE,"E25.0");var subQ6=sQuery(id+"F0.wireOp",EDGE,"E25.2");var subQ7=sQuery(id+"F0.wireOp",EDGE,"E25.3");Q4=makeQuery(id+"F8.boolean.opBoolean","INTERSECT",EDGE,{"derivedFrom":[makeQuery(id+"F5.boolean.opBoolean","SPLIT",FACE,{"disambiguationData":[TD([makeQuery(id+"F2.opExtrude","SWEPT_FACE",FACE,{"disambiguationData":[OSD([subQ5])]})])],"derivedFrom":makeQuery(id+"F3.boolean.opBoolean","COPY",FACE,{"derivedFrom":makeQuery(id+"F3.opExtrude","CAP_FACE",FACE,{"disambiguationData":[OSD([subQ5,subQ1,subQ6,subQ7,subQ4,subQ3,subQ2,subQ0])],"isStart":false})})}),makeQuery(id+"F8.opExtrude","SWEPT_FACE",FACE,{"disambiguationData":[OSD([sQuery(id+"F7.wireOp",EDGE,"E67")])]})]});}
            var Q5;
            Q5=makeQuery(id+"F8.boolean.opBoolean","INTERSECT",EDGE,{"disambiguationData":[OD(0.0)],"derivedFrom":[makeQuery(id+"F5.opExtrude","SWEPT_FACE",FACE,{"disambiguationData":[OSD([sQuery(id+"F4.wireOp",EDGE,"E30")])]}),makeQuery(id+"F8.opExtrude","SWEPT_FACE",FACE,{"disambiguationData":[OSD([sQuery(id+"F7.wireOp",EDGE,"E67")])]})]});
            fillet(context, id + "F14", {"entities" : qUnion([Q0, Q1, Q2, Q3, Q4, Q5]), "radius" : 3 * mm, "tangentPropagation" : true, "allowEdgeOverflow" : false});
        }
        {
            var Q0;
            Q0=makeQuery(id+"F1.opExtrude","CAP_EDGE",EDGE,{"disambiguationData":[OSD([sQuery(id+"F0.wireOp",EDGE,"E1.bottom")])],"isStart":false});
            fillet(context, id + "F15", {"entities" : qUnion([Q0]), "radius" : 2 * mm, "tangentPropagation" : true, "allowEdgeOverflow" : false});
        }
        {
            var Q0;
            {var subQ0=sQuery(id+"F0.wireOp",EDGE,"E21.filletArc");var subQ1=sQuery(id+"F0.wireOp",EDGE,"E7");var subQ2=sQuery(id+"F0.wireOp",EDGE,"E6");var subQ3=sQuery(id+"F0.wireOp",EDGE,"E5");var subQ4=sQuery(id+"F0.wireOp",EDGE,"E4");var subQ5=sQuery(id+"F0.wireOp",EDGE,"E22.filletArc");var subQ6=sQuery(id+"F0.wireOp",EDGE,"E1.bottom");var subQ7=sQuery(id+"F0.wireOp",EDGE,"E1.right");var subQ8=sQuery(id+"F0.wireOp",EDGE,"E1.top");var subQ9=sQuery(id+"F0.wireOp",EDGE,"E1.left");var subQ10=sQuery(id+"F0.wireOp",EDGE,"E23.filletArc");var subQ11=sQuery(id+"F0.wireOp",EDGE,"E24.filletArc");Q0=makeQuery(id+"F2.boolean.opBoolean","SPLIT",FACE,{"disambiguationData":[TD([makeQuery(id+"F1.opExtrude","SWEPT_FACE",FACE,{"disambiguationData":[OSD([subQ6])]})])],"derivedFrom":makeQuery(id+"F1.opExtrude","CAP_FACE",FACE,{"disambiguationData":[OSD([subQ6,subQ8,subQ9,subQ7,subQ4,subQ3,subQ2,subQ1,subQ0,subQ5,subQ10,subQ11])],"isStart":true})});}
            var sketch = newSketch(context, id + "F16", { "sketchPlane" : qUnion([Q0])});
            skLineSegment(sketch, "E79", {"start": v(0, 90) * mm, "end": v(0, 120) * mm, "construction": true});
            skLineSegment(sketch, "E80", {"start": v(-33, 90) * mm, "end": v(-15, 108) * mm});
            skLineSegment(sketch, "E81", {"start": v(-15, 108) * mm, "end": v(-15, 120) * mm});
            skLineSegment(sketch, "E82", {"start": v(33, 90) * mm, "end": v(15, 108) * mm});
            skLineSegment(sketch, "E83", {"start": v(15, 108) * mm, "end": v(15, 120) * mm});
            skArc(sketch, "E84", {"start": v(15, 120) * mm, "mid": v(0, 135) * mm, "end": v(-15, 120) * mm});
            skCircle(sketch, "E85", {"center": v(0, 120) * mm, "radius": 6 * mm});
            skLineSegment(sketch, "E86", {"start": v(-80, 0) * mm, "end": v(80, 0) * mm, "construction": true});
            skLineSegment(sketch, "E87.MirrorCS", {"start": v(33, -90) * mm, "end": v(15, -108) * mm});
            skLineSegment(sketch, "E88.MirrorCS", {"start": v(-33, -90) * mm, "end": v(-15, -108) * mm});
            skLineSegment(sketch, "E89.MirrorCS", {"start": v(-15, -108) * mm, "end": v(-15, -120) * mm});
            skLineSegment(sketch, "E90.MirrorCS", {"start": v(15, -108) * mm, "end": v(15, -120) * mm});
            skArc(sketch, "E91.MirrorCS", {"start": v(15, -120) * mm, "mid": v(0, -135) * mm, "end": v(-15, -120) * mm});
            skCircle(sketch, "E92.MirrorC", {"center": v(0, -120) * mm, "radius": 6 * mm});
            skLineSegment(sketch, "E93.MirrorCS", {"start": v(0, -90) * mm, "end": v(0, -120) * mm, "construction": true});
            skSolve(sketch);
        }
        {
            var Q0;
            {var subQ1=sQuery(id+"F16.wireOp",EDGE,"E87.MirrorCS");Q0=makeQuery(id+"F16.imprint","IMPRINT",FACE,{"disambiguationData":[TD([[makeQuery(id+"F16.imprint","IMPRINT",EDGE,{"derivedFrom":subQ1}),-1.0]])]});}
            var Q1;
            Q1=makeQuery(id+"F16.imprint","IMPRINT",FACE,{"disambiguationData":[TD([[makeQuery(id+"F16.imprint","IMPRINT",EDGE,{"derivedFrom":makeQuery(id+"F1.opExtrude","CAP_EDGE",EDGE,{"disambiguationData":[OSD([sQuery(id+"F0.wireOp",EDGE,"E1.left")])],"isStart":true})}),-1.0]])]});
            var Q2;
            {var subQ1=sQuery(id+"F16.wireOp",EDGE,"E80");Q2=makeQuery(id+"F16.imprint","IMPRINT",FACE,{"disambiguationData":[TD([[makeQuery(id+"F16.imprint","IMPRINT",EDGE,{"derivedFrom":subQ1}),-1.0]])]});}
            var Q3;
            Q3=makeQuery(id+"F2.opExtrude","CAP_FACE",FACE,{"disambiguationData":[OSD([sQuery(id+"F0.wireOp",EDGE,"E12"),sQuery(id+"F0.wireOp",EDGE,"E13"),sQuery(id+"F0.wireOp",EDGE,"E14"),sQuery(id+"F0.wireOp",EDGE,"E15"),sQuery(id+"F0.wireOp",EDGE,"E17.filletArc"),sQuery(id+"F0.wireOp",EDGE,"E18.filletArc"),sQuery(id+"F0.wireOp",EDGE,"E19.filletArc"),sQuery(id+"F0.wireOp",EDGE,"E20.filletArc"),sQuery(id+"F0.wireOp",EDGE,"E25.0"),sQuery(id+"F0.wireOp",EDGE,"E25.1"),sQuery(id+"F0.wireOp",EDGE,"E25.2"),sQuery(id+"F0.wireOp",EDGE,"E25.3"),sQuery(id+"F0.wireOp",EDGE,"E25.4"),sQuery(id+"F0.wireOp",EDGE,"E25.5"),sQuery(id+"F0.wireOp",EDGE,"E25.6"),sQuery(id+"F0.wireOp",EDGE,"E25.7")])],"isStart":false});
            extrude(context, id + "F17", {"entities" : qUnion([Q0, Q1, Q2]), "endBound" : BoundingType.UP_TO_SURFACE, "endBoundEntityFace" : qUnion([Q3]), "depth" : 25 * mm});
        }
    });
